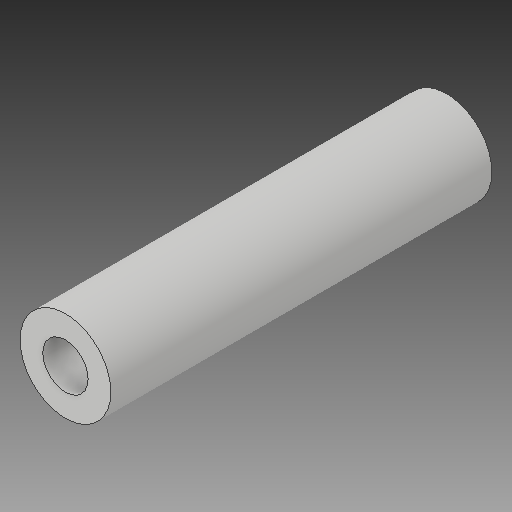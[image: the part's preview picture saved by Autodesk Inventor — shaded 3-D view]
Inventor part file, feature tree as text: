
AUTODESK INVENTOR PART (.ipt)
format: ipt  version: 2019 (Build 230136000, 136)  size: 95,232 bytes
history: native  units: in
note: dims shown in document units (in); Inventor stores cm internally (conversion verified against a paired STEP export)
features: extrude x1, sketch x1
ambient origin geometry x8: Origin, YZ Plane, XZ Plane, XY Plane, X Axis, Y Axis, Z Axis, Center Point
bodies: Solid1 (feature_tree)
feature tree (2):
  extrude  "Extrusion1"  Depth=0.125in
  sketch  "Sketch1"  dims[d0=0.25in d1=0.125in d2=1.05in d3=0.0in]
